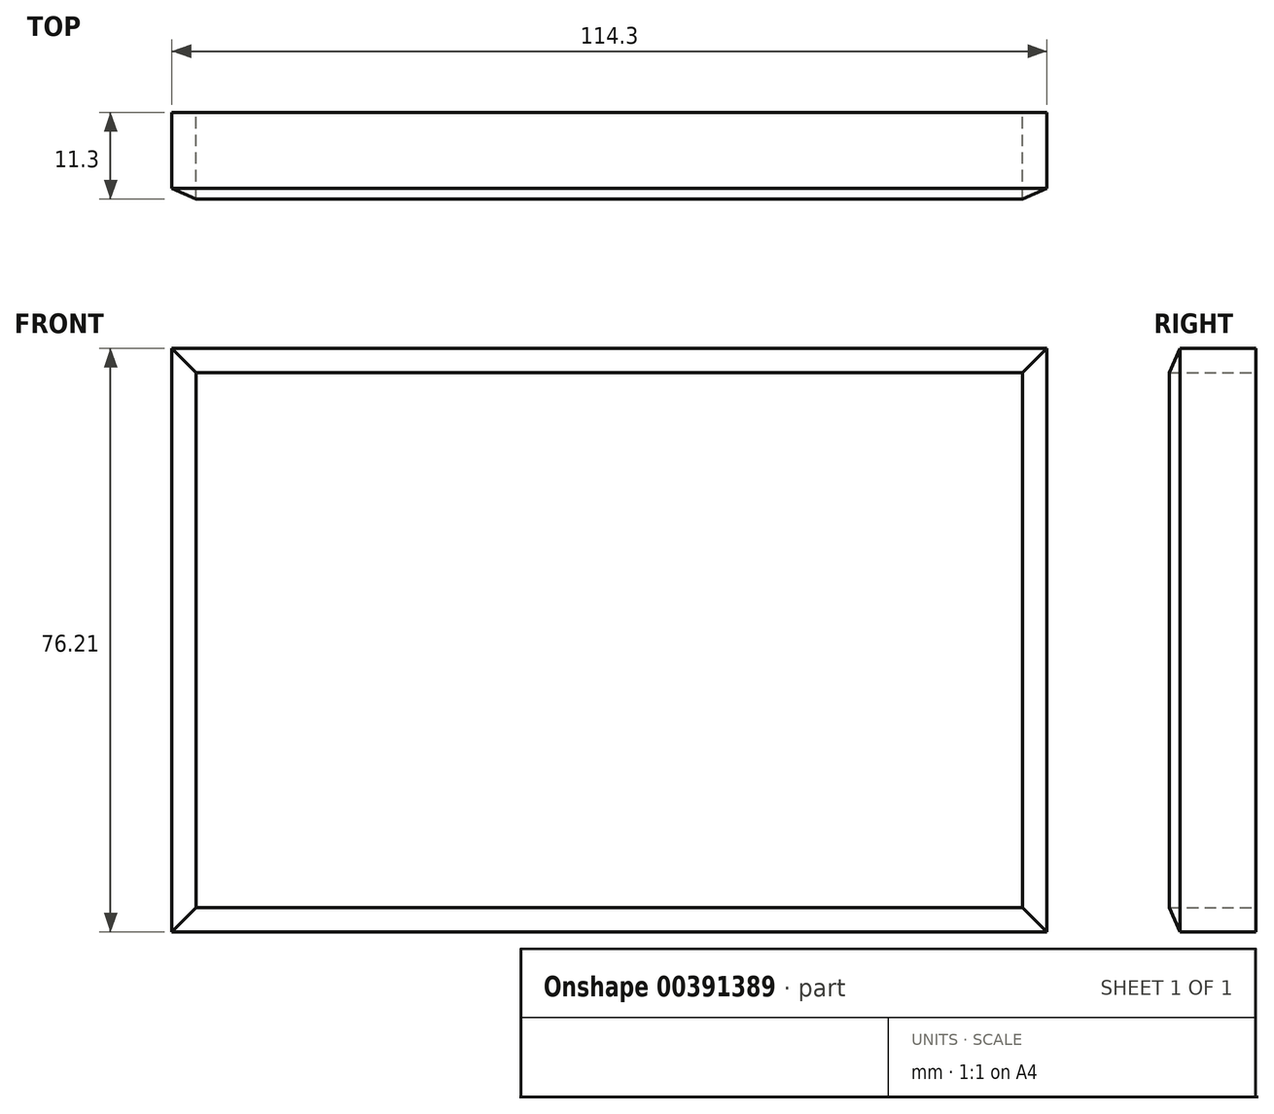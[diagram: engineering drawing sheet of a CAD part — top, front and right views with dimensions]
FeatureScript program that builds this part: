
annotation { "Feature Type Name" : "Feature", "Feature Type Description" : "" }
export const myFeature = defineFeature(function(context is Context, id is Id, definition is map)
    precondition{}
    {
        {
            var Q0;
            Q0=qCreatedBy(makeId("Front.planeOp"),FACE);
            var sketch = newSketch(context, id + "F0", { "sketchPlane" : qUnion([Q0])});
            skLineSegment(sketch, "E0.bottom", {"start": v(-0.85, 0) * mm, "end": v(107.1, 0) * mm});
            skLineSegment(sketch, "E0.top", {"start": v(-0.85, 69.85) * mm, "end": v(107.1, 69.85) * mm});
            skLineSegment(sketch, "E0.left", {"start": v(-0.85, 0) * mm, "end": v(-0.85, 69.85) * mm});
            skLineSegment(sketch, "E0.right", {"start": v(107.1, 0) * mm, "end": v(107.1, 69.85) * mm});
            skLineSegment(sketch, "E1.0", {"start": v(-4.03, 73.03) * mm, "end": v(110.27, 73.03) * mm});
            skLineSegment(sketch, "E1.1", {"start": v(-4.03, -3.17) * mm, "end": v(-4.03, 73.03) * mm});
            skLineSegment(sketch, "E1.2", {"start": v(-4.03, -3.17) * mm, "end": v(110.27, -3.17) * mm});
            skLineSegment(sketch, "E1.3", {"start": v(110.27, -3.17) * mm, "end": v(110.27, 73.03) * mm});
            skSolve(sketch);
        }
        {
            var Q0;
            Q0=qSketchRegion(id+"F0",true);
            extrude(context, id + "F1", {"entities" : qUnion([Q0]), "depth" : 12.7 * mm});
        }
        {
            var Q0;
            Q0=makeQuery(id+"F1.opExtrude","CAP_EDGE",EDGE,{"disambiguationData":[OSD([sQuery(id+"F0.wireOp",EDGE,"E1.0")])],"isStart":false});
            var Q1;
            Q1=makeQuery(id+"F1.opExtrude","CAP_EDGE",EDGE,{"disambiguationData":[OSD([sQuery(id+"F0.wireOp",EDGE,"E1.3")])],"isStart":false});
            var Q2;
            Q2=makeQuery(id+"F1.opExtrude","CAP_EDGE",EDGE,{"disambiguationData":[OSD([sQuery(id+"F0.wireOp",EDGE,"E1.1")])],"isStart":false});
            var Q3;
            Q3=makeQuery(id+"F1.opExtrude","CAP_EDGE",EDGE,{"disambiguationData":[OSD([sQuery(id+"F0.wireOp",EDGE,"E1.2")])],"isStart":false});
            chamfer(context, id + "F2", {"entities" : qUnion([Q0, Q1, Q2, Q3]), "chamferType" : ChamferType.TWO_OFFSETS, "width1" : 6.35 * mm, "oppositeDirection" : false, "width2" : 2.8 * mm, "tangentPropagation" : true});
        }
    });
